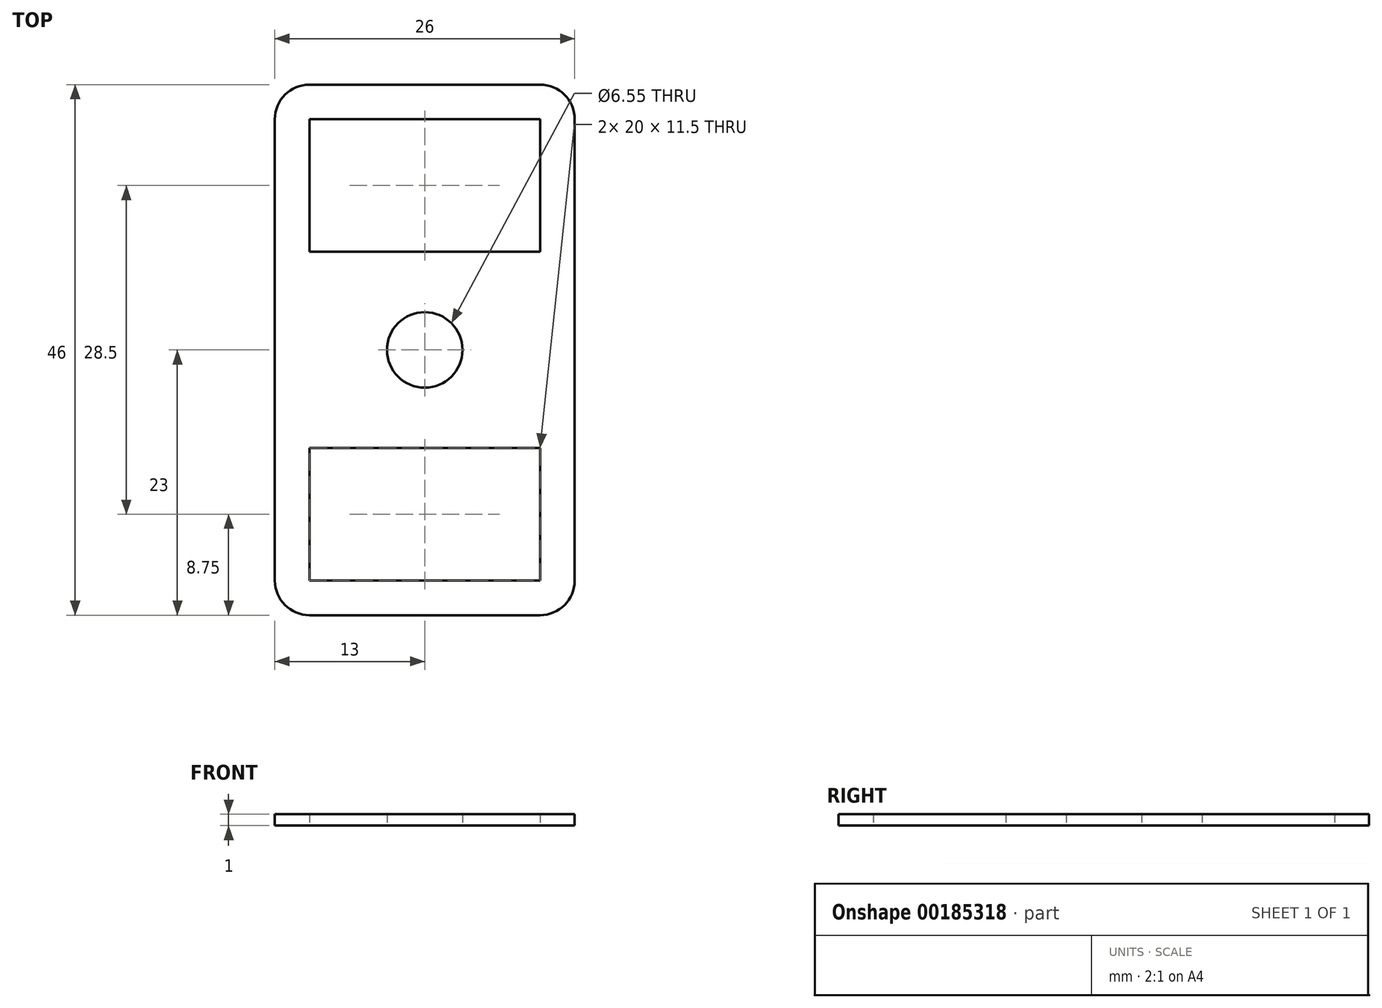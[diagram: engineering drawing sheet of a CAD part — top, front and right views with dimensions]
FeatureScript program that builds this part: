
annotation { "Feature Type Name" : "Feature", "Feature Type Description" : "" }
export const myFeature = defineFeature(function(context is Context, id is Id, definition is map)
    precondition{}
    {
        {
            var Q0;
            Q0=qCreatedBy(makeId("Top.planeOp"),FACE);
            var sketch = newSketch(context, id + "F0", { "sketchPlane" : qUnion([Q0])});
            skCircle(sketch, "E0", {"center": v(0, 0) * mm, "radius": 3.28 * mm});
            skLineSegment(sketch, "E1.bottom", {"start": v(-10, 20) * mm, "end": v(10, 20) * mm});
            skLineSegment(sketch, "E1.top", {"start": v(-10, 8.5) * mm, "end": v(10, 8.5) * mm});
            skLineSegment(sketch, "E1.left", {"start": v(-10, 20) * mm, "end": v(-10, 8.5) * mm});
            skLineSegment(sketch, "E1.right", {"start": v(10, 20) * mm, "end": v(10, 8.5) * mm});
            skLineSegment(sketch, "E2.0", {"start": v(-13, 23) * mm, "end": v(-13, 8.5) * mm});
            skLineSegment(sketch, "E2.1", {"start": v(-13, 23) * mm, "end": v(13, 23) * mm});
            skLineSegment(sketch, "E2.2", {"start": v(13, 23) * mm, "end": v(13, 8.5) * mm});
            skLineSegment(sketch, "E3", {"start": v(-13, 8.5) * mm, "end": v(-13, 0) * mm});
            skLineSegment(sketch, "E4", {"start": v(13, 8.5) * mm, "end": v(13, 0) * mm});
            skLineSegment(sketch, "E5.MirrorCS", {"start": v(-13, -8.5) * mm, "end": v(-13, 0) * mm});
            skLineSegment(sketch, "E6.MirrorCS", {"start": v(-13, -23) * mm, "end": v(-13, -8.5) * mm});
            skLineSegment(sketch, "E7.MirrorCS", {"start": v(-13, -23) * mm, "end": v(13, -23) * mm});
            skLineSegment(sketch, "E8.MirrorCS", {"start": v(13, -23) * mm, "end": v(13, -8.5) * mm});
            skLineSegment(sketch, "E9.MirrorCS", {"start": v(13, -8.5) * mm, "end": v(13, 0) * mm});
            skLineSegment(sketch, "E10.MirrorCS", {"start": v(-10, -8.5) * mm, "end": v(10, -8.5) * mm});
            skLineSegment(sketch, "E11.MirrorCS", {"start": v(-10, -20) * mm, "end": v(-10, -8.5) * mm});
            skLineSegment(sketch, "E12.MirrorCS", {"start": v(-10, -20) * mm, "end": v(10, -20) * mm});
            skLineSegment(sketch, "E13.MirrorCS", {"start": v(10, -20) * mm, "end": v(10, -8.5) * mm});
            skSolve(sketch);
        }
        {
            var Q0;
            Q0 = qSketchRegion(id + "F0", true);
            extrude(context, id + "F1", {"entities" : qUnion([Q0]), "depth" : 1 * mm});
        }
        {
            var Q0;
            Q0=makeQuery(id+"F1.opExtrude","SWEPT_EDGE",EDGE,{"disambiguationData":[OSD([sQuery(id+"F0.wireOp",EDGE,"E7.MirrorCS"),sQuery(id+"F0.wireOp",EDGE,"E8.MirrorCS")])]});
            var Q1;
            Q1=makeQuery(id+"F1.opExtrude","SWEPT_EDGE",EDGE,{"disambiguationData":[OSD([sQuery(id+"F0.wireOp",EDGE,"E6.MirrorCS"),sQuery(id+"F0.wireOp",EDGE,"E7.MirrorCS")])]});
            var Q2;
            Q2=makeQuery(id+"F1.opExtrude","SWEPT_EDGE",EDGE,{"disambiguationData":[OSD([sQuery(id+"F0.wireOp",EDGE,"E2.1"),sQuery(id+"F0.wireOp",EDGE,"E2.2")])]});
            var Q3;
            Q3=makeQuery(id+"F1.opExtrude","SWEPT_EDGE",EDGE,{"disambiguationData":[OSD([sQuery(id+"F0.wireOp",EDGE,"E2.0"),sQuery(id+"F0.wireOp",EDGE,"E2.1")])]});
            fillet(context, id + "F2", {"entities" : qUnion([Q0, Q1, Q2, Q3]), "radius" : 3 * mm, "allowEdgeOverflow" : false});
        }
    });
